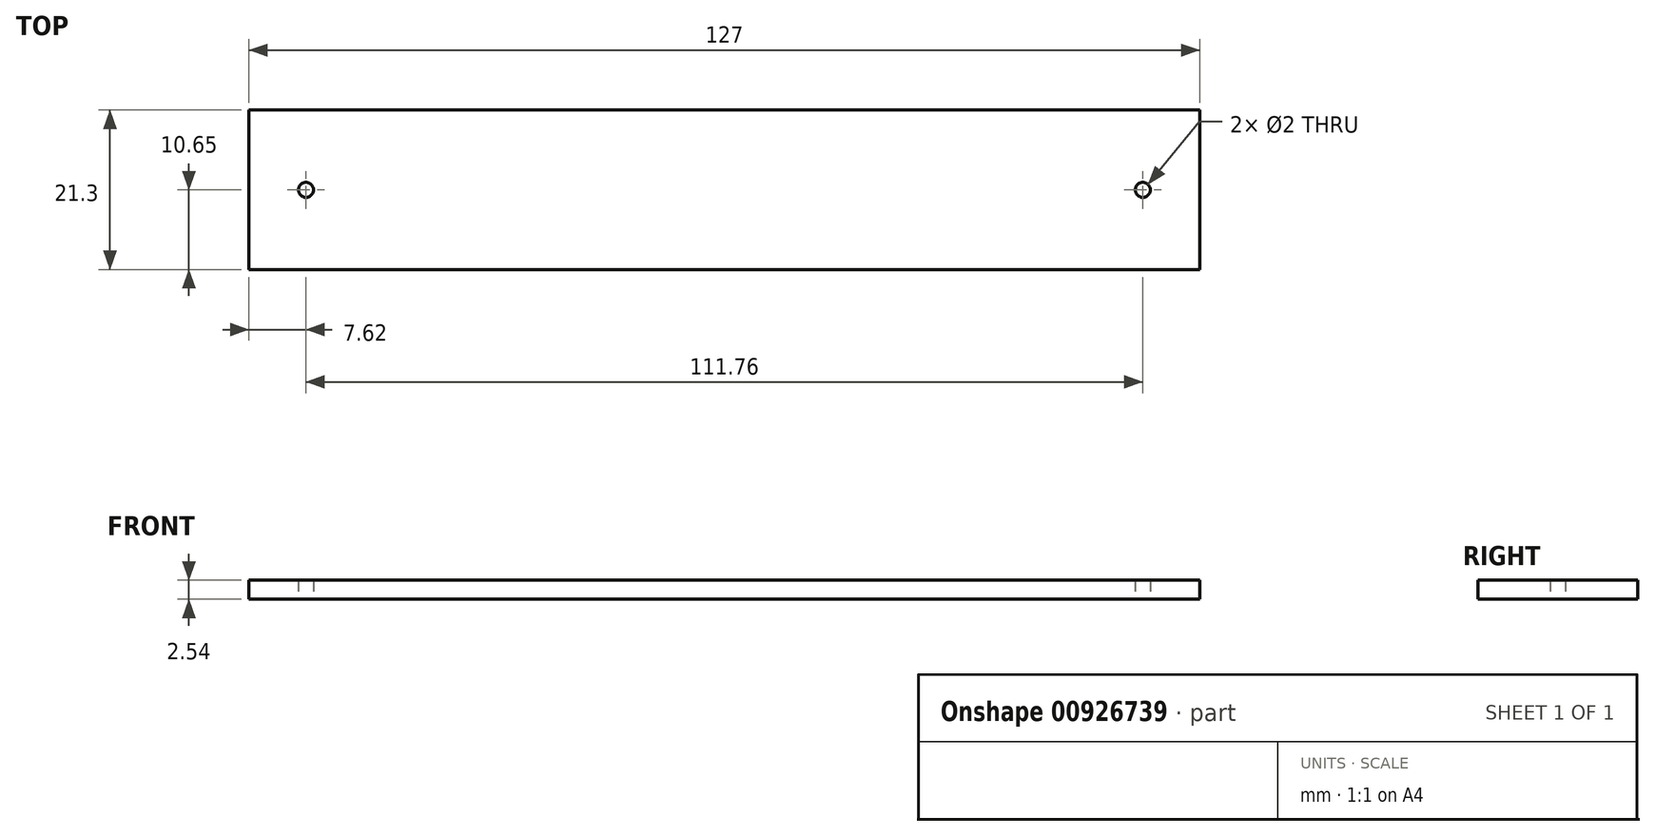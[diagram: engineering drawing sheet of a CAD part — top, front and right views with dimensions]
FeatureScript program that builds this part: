
annotation { "Feature Type Name" : "Feature", "Feature Type Description" : "" }
export const myFeature = defineFeature(function(context is Context, id is Id, definition is map)
    precondition{}
    {
        {
            var Q0;
            Q0=qCreatedBy(makeId("Top.planeOp"),FACE);
            var sketch = newSketch(context, id + "F0", { "sketchPlane" : qUnion([Q0])});
            skLineSegment(sketch, "E0.bottom", {"start": v(63.5, 10.65) * mm, "end": v(-63.5, 10.65) * mm});
            skLineSegment(sketch, "E0.top", {"start": v(63.5, -10.65) * mm, "end": v(-63.5, -10.65) * mm});
            skLineSegment(sketch, "E0.left", {"start": v(63.5, 10.65) * mm, "end": v(63.5, -10.65) * mm});
            skLineSegment(sketch, "E0.right", {"start": v(-63.5, 10.65) * mm, "end": v(-63.5, -10.65) * mm});
            skPoint(sketch, "E0.middle", {"position": v(0, 0) * mm});
            skCircle(sketch, "E1", {"center": v(-55.88, 0) * mm, "radius": 1 * mm});
            skCircle(sketch, "E2", {"center": v(55.88, 0) * mm, "radius": 1 * mm});
            skSolve(sketch);
        }
        {
            var Q0;
            Q0=makeQuery(id+"F0.imprint","IMPRINT",FACE,{"disambiguationData":[TD([[makeQuery(id+"F0.imprint","IMPRINT",EDGE,{"derivedFrom":sQuery(id+"F0.wireOp",EDGE,"E0.bottom")}),1.0]])]});
            extrude(context, id + "F1", {"entities" : qUnion([Q0]), "endBound" : BoundingType.SYMMETRIC, "depth" : 2.54 * mm, "offsetDistance" : 25.4 * mm});
        }
    });
